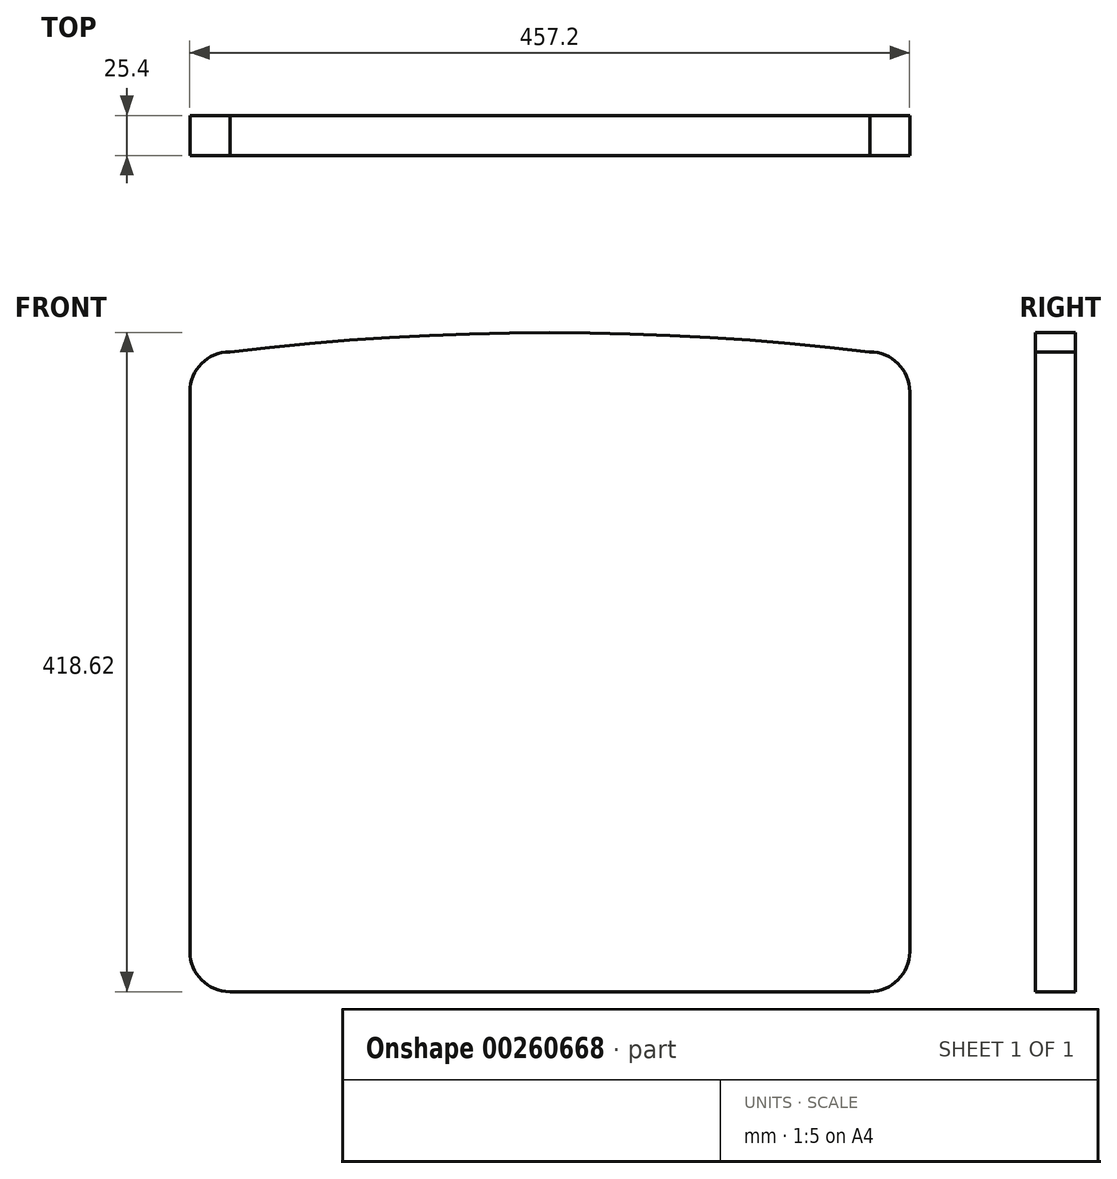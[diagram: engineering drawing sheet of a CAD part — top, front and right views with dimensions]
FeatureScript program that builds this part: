
annotation { "Feature Type Name" : "Feature", "Feature Type Description" : "" }
export const myFeature = defineFeature(function(context is Context, id is Id, definition is map)
    precondition{}
    {
        {
            var Q0;
            Q0=qCreatedBy(makeId("Front.planeOp"),FACE);
            var sketch = newSketch(context, id + "F0", { "sketchPlane" : qUnion([Q0])});
            skLineSegment(sketch, "E0.bottom", {"start": v(-163.78, 186.35) * mm, "end": v(242.62, 186.35) * mm});
            skLineSegment(sketch, "E0.top", {"start": v(-163.78, -220.05) * mm, "end": v(242.62, -220.05) * mm});
            skLineSegment(sketch, "E0.left", {"start": v(-189.18, 160.95) * mm, "end": v(-189.18, -194.65) * mm});
            skLineSegment(sketch, "E0.right", {"start": v(268.02, 160.95) * mm, "end": v(268.02, -194.65) * mm});
            skPoint(sketch, "E1.visualSharp", {"position": v(-189.18, -220.05) * mm});
            skArc(sketch, "E1.filletArc", {"start": v(-189.18, -194.65) * mm, "mid": v(-181.74, -212.62) * mm, "end": v(-163.78, -220.05) * mm});
            skPoint(sketch, "E2.visualSharp", {"position": v(268.02, -220.05) * mm});
            skArc(sketch, "E2.filletArc", {"start": v(242.62, -220.05) * mm, "mid": v(260.58, -212.62) * mm, "end": v(268.02, -194.65) * mm});
            skPoint(sketch, "E3.visualSharp", {"position": v(-189.18, 186.35) * mm});
            skArc(sketch, "E3.filletArc", {"start": v(-163.78, 186.35) * mm, "mid": v(-181.74, 178.9) * mm, "end": v(-189.18, 160.95) * mm});
            skPoint(sketch, "E4.visualSharp", {"position": v(268.02, 186.35) * mm});
            skArc(sketch, "E4.filletArc", {"start": v(268.02, 160.95) * mm, "mid": v(260.58, 178.9) * mm, "end": v(242.62, 186.35) * mm});
            skArc(sketch, "E5", {"start": v(242.62, 186.35) * mm, "mid": v(39.42, 198.57) * mm, "end": v(-163.78, 186.35) * mm});
            skSolve(sketch);
        }
        {
            var Q0;
            Q0 = qSketchRegion(id + "F0", true);
            extrude(context, id + "F1", {"entities" : qUnion([Q0]), "depth" : 25.4 * mm});
        }
    });
